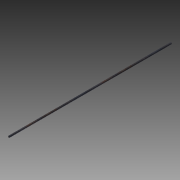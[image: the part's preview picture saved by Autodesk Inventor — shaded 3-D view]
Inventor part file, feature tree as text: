
AUTODESK INVENTOR PART (.ipt)
format: ipt  version: 2011 SP1 (Build 150282100, 282)  size: 68,096 bytes
history: native  units: in
note: dims shown in document units (in); Inventor stores cm internally (conversion verified against a paired STEP export)
features: extrude x1, fillet x1, sketch x1
ambient origin geometry x8: Origin, YZ Plane, XZ Plane, XY Plane, X Axis, Y Axis, Z Axis, Center Point
bodies: Solid1 (feature_tree)
feature tree (3):
  extrude  "Extrusion1"  Depth=8.5in TaperAngle=0.0deg
  fillet  "Fillet1"  Radius=0.001in
  sketch  "Sketch1"  dims[d0=0.089in d1=8.5in d2=0.0in d3=0.001in]
